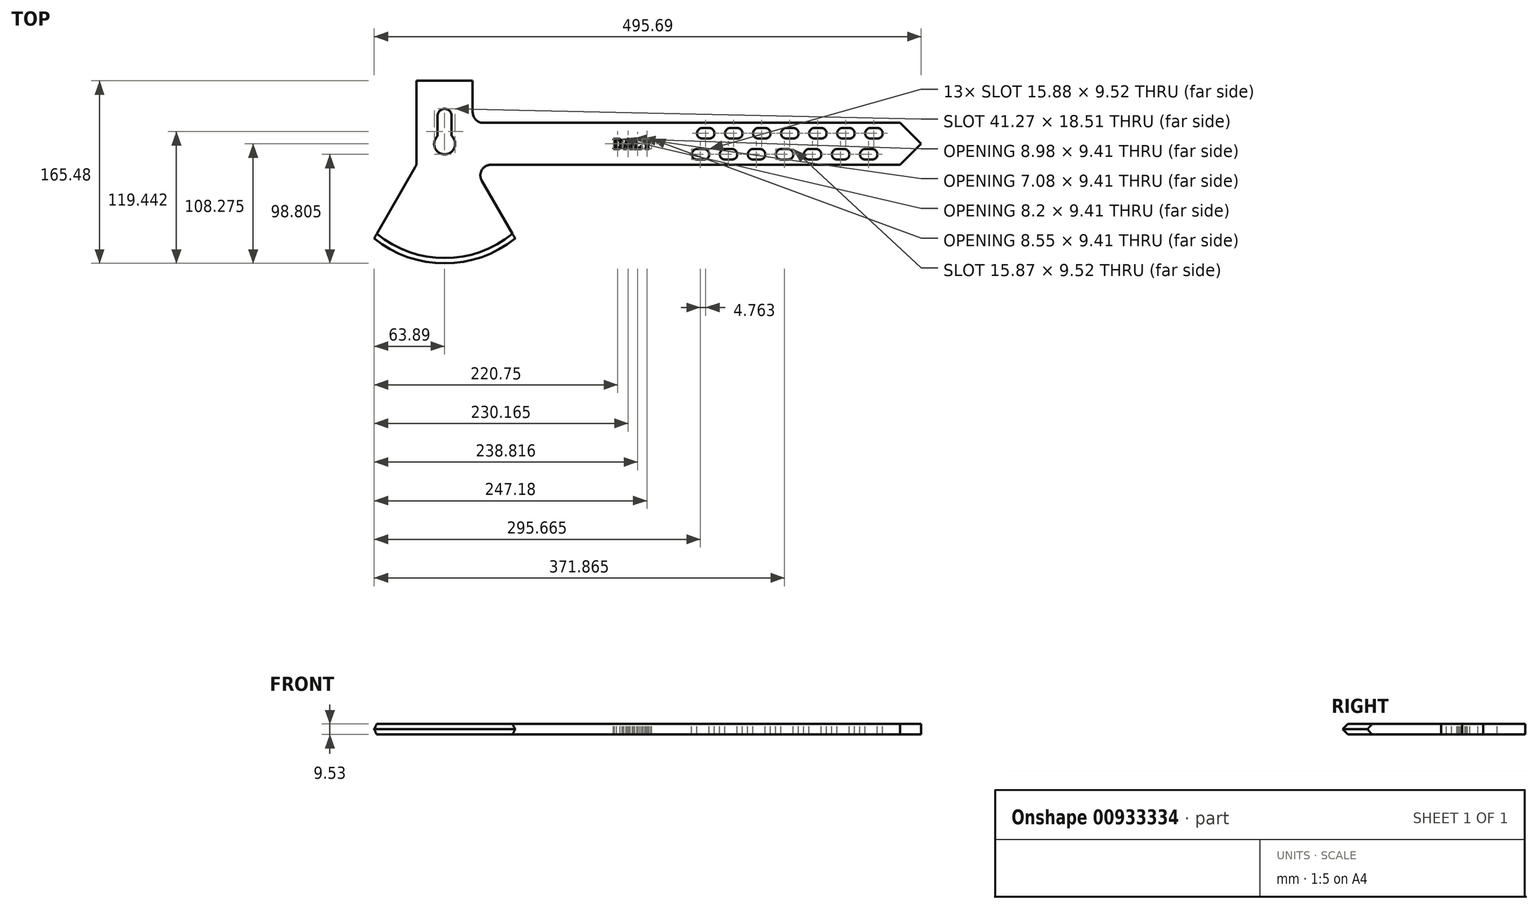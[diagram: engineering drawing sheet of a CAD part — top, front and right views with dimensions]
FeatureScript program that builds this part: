
annotation { "Feature Type Name" : "Feature", "Feature Type Description" : "" }
export const myFeature = defineFeature(function(context is Context, id is Id, definition is map)
    precondition{}
    {
        {
            var Q0;
            Q0=qCreatedBy(makeId("Top.planeOp"),FACE);
            var sketch = newSketch(context, id + "F0", { "sketchPlane" : qUnion([Q0])});
            skLineSegment(sketch, "E0", {"start": v(0, 0) * mm, "end": v(-19.05, 19.05) * mm});
            skLineSegment(sketch, "E1", {"start": v(-19.05, 19.05) * mm, "end": v(-406.4, 19.05) * mm});
            skLineSegment(sketch, "E2", {"start": v(0, 0) * mm, "end": v(-457.2, 0) * mm, "construction": true});
            skLineSegment(sketch, "E3", {"start": v(-457.2, 0) * mm, "end": v(-457.2, 57.15) * mm});
            skLineSegment(sketch, "E4", {"start": v(-457.2, 57.15) * mm, "end": v(-406.4, 57.15) * mm});
            skLineSegment(sketch, "E5", {"start": v(-406.4, 57.15) * mm, "end": v(-406.4, 19.05) * mm});
            skLineSegment(sketch, "E6.MirrorCS", {"start": v(-19.05, -19.05) * mm, "end": v(-406.4, -19.05) * mm});
            skLineSegment(sketch, "E7.MirrorCS", {"start": v(0, 0) * mm, "end": v(-19.05, -19.05) * mm});
            skLineSegment(sketch, "E8", {"start": v(-431.8, 57.15) * mm, "end": v(-431.8, -6.73) * mm, "construction": true});
            skLineSegment(sketch, "E9", {"start": v(-406.4, -19.05) * mm, "end": v(-367.9, -85.73) * mm});
            skLineSegment(sketch, "E10", {"start": v(-457.2, 0) * mm, "end": v(-457.2, -19.05) * mm});
            skLineSegment(sketch, "E11", {"start": v(-457.2, -19.05) * mm, "end": v(-495.7, -85.73) * mm});
            skArc(sketch, "E12", {"start": v(-495.7, -85.73) * mm, "mid": v(-431.8, -108.33) * mm, "end": v(-367.9, -85.73) * mm});
            skSolve(sketch);
        }
        {
            var Q0;
            Q0 = qSketchRegion(id + "F0", true);
            extrude(context, id + "F1", {"entities" : qUnion([Q0]), "depth" : 9.52 * mm, "offsetDistance" : 25.4 * mm});
        }
        {
            var Q0;
            Q0=makeQuery(id+"F1.opExtrude","CAP_FACE",FACE,{"disambiguationData":[OSD([sQuery(id+"F0.wireOp",EDGE,"E0"),sQuery(id+"F0.wireOp",EDGE,"E1"),sQuery(id+"F0.wireOp",EDGE,"E3"),sQuery(id+"F0.wireOp",EDGE,"E4"),sQuery(id+"F0.wireOp",EDGE,"E5"),sQuery(id+"F0.wireOp",EDGE,"E6.MirrorCS"),sQuery(id+"F0.wireOp",EDGE,"E7.MirrorCS"),sQuery(id+"F0.wireOp",EDGE,"E9"),sQuery(id+"F0.wireOp",EDGE,"E10"),sQuery(id+"F0.wireOp",EDGE,"E11"),sQuery(id+"F0.wireOp",EDGE,"E12")])],"isStart":false});
            var sketch = newSketch(context, id + "F2", { "sketchPlane" : qUnion([Q0])});
            skText(sketch, "E13", { "text": "DALY", "fontName": "RobotoSlab-Bold.ttf"});
            skPoint(sketch, "E14", {"position": v(-243.44, 0) * mm});
            skLineSegment(sketch, "E15", {"start": v(-243.44, 0) * mm, "end": v(0, 0) * mm});
            const initialGuessF2  = {"E13": [-0.2794, -0.00476, 1, 0, 0.00953]};
            skSetInitialGuess(sketch, initialGuessF2);
            skSolve(sketch);
        }
        {
            var Q0;
            Q0 = qSketchRegion(id + "F2", true);
            extrude(context, id + "F3", {"entities" : qUnion([Q0]), "operationType" : NewBodyOperationType.REMOVE, "oppositeDirection" : true, "depth" : 25.4 * mm, "offsetDistance" : 25.4 * mm});
        }
        {
            var Q0;
            {var subQ0=sQuery(id+"F0.wireOp",EDGE,"E11");var subQ1=sQuery(id+"F0.wireOp",EDGE,"E9");var subQ2=sQuery(id+"F0.wireOp",EDGE,"E7.MirrorCS");var subQ3=sQuery(id+"F0.wireOp",EDGE,"E6.MirrorCS");var subQ4=sQuery(id+"F0.wireOp",EDGE,"E5");var subQ5=sQuery(id+"F0.wireOp",EDGE,"E12");var subQ6=sQuery(id+"F0.wireOp",EDGE,"E0");var subQ7=sQuery(id+"F0.wireOp",EDGE,"E4");var subQ8=sQuery(id+"F0.wireOp",EDGE,"E1");var subQ9=sQuery(id+"F0.wireOp",EDGE,"E10");var subQ10=sQuery(id+"F0.wireOp",EDGE,"E3");Q0=makeQuery(id+"F3.boolean.opBoolean","SPLIT",FACE,{"disambiguationData":[TD([makeQuery(id+"F1.opExtrude","SWEPT_FACE",FACE,{"disambiguationData":[OSD([subQ6])]})])],"derivedFrom":makeQuery(id+"F1.opExtrude","CAP_FACE",FACE,{"disambiguationData":[OSD([subQ6,subQ8,subQ10,subQ7,subQ4,subQ3,subQ2,subQ1,subQ9,subQ0,subQ5])],"isStart":false})});}
            var sketch = newSketch(context, id + "F4", { "sketchPlane" : qUnion([Q0])});
            skLineSegment(sketch, "E16", {"start": v(0, 0) * mm, "end": v(-203.2, 0) * mm, "construction": true});
            skLineSegment(sketch, "E17", {"start": v(-198.44, 9.52) * mm, "end": v(-192.09, 9.52) * mm});
            skLineSegment(sketch, "E18", {"start": v(-203.2, -9.53) * mm, "end": v(-196.85, -9.53) * mm});
            skArc(sketch, "E19.0.startCap", {"start": v(-198.44, 4.76) * mm, "mid": v(-203.2, 9.52) * mm, "end": v(-198.44, 14.29) * mm});
            skArc(sketch, "E19.0.endCap", {"start": v(-192.09, 14.29) * mm, "mid": v(-187.33, 9.52) * mm, "end": v(-192.09, 4.76) * mm});
            skLineSegment(sketch, "E19.0.left", {"start": v(-198.44, 14.29) * mm, "end": v(-192.09, 14.29) * mm});
            skLineSegment(sketch, "E19.0.right", {"start": v(-198.44, 4.76) * mm, "end": v(-192.09, 4.76) * mm});
            skArc(sketch, "E19.1.startCap", {"start": v(-203.2, -14.29) * mm, "mid": v(-207.96, -9.53) * mm, "end": v(-203.2, -4.76) * mm});
            skArc(sketch, "E19.1.endCap", {"start": v(-196.85, -4.76) * mm, "mid": v(-192.09, -9.53) * mm, "end": v(-196.85, -14.29) * mm});
            skLineSegment(sketch, "E19.1.left", {"start": v(-203.2, -4.76) * mm, "end": v(-196.85, -4.76) * mm});
            skLineSegment(sketch, "E19.1.right", {"start": v(-203.2, -14.29) * mm, "end": v(-196.85, -14.29) * mm});
            skArc(sketch, "E20.1.0.0", {"start": v(-166.69, 14.29) * mm, "mid": v(-161.93, 9.52) * mm, "end": v(-166.69, 4.76) * mm});
            skLineSegment(sketch, "E20.1.0.1", {"start": v(-173.04, 14.29) * mm, "end": v(-166.69, 14.29) * mm});
            skArc(sketch, "E20.1.0.2", {"start": v(-173.04, 4.76) * mm, "mid": v(-177.8, 9.52) * mm, "end": v(-173.04, 14.29) * mm});
            skLineSegment(sketch, "E20.1.0.3", {"start": v(-173.04, 4.76) * mm, "end": v(-166.69, 4.76) * mm});
            skLineSegment(sketch, "E20.1.0.4", {"start": v(-177.8, -4.76) * mm, "end": v(-171.45, -4.76) * mm});
            skArc(sketch, "E20.1.0.5", {"start": v(-171.45, -4.76) * mm, "mid": v(-166.69, -9.53) * mm, "end": v(-171.45, -14.29) * mm});
            skLineSegment(sketch, "E20.1.0.6", {"start": v(-177.8, -14.29) * mm, "end": v(-171.45, -14.29) * mm});
            skArc(sketch, "E20.1.0.7", {"start": v(-177.8, -14.29) * mm, "mid": v(-182.56, -9.53) * mm, "end": v(-177.8, -4.76) * mm});
            skArc(sketch, "E20.2.0.0", {"start": v(-141.29, 14.29) * mm, "mid": v(-136.53, 9.52) * mm, "end": v(-141.29, 4.76) * mm});
            skLineSegment(sketch, "E20.2.0.1", {"start": v(-147.64, 14.29) * mm, "end": v(-141.29, 14.29) * mm});
            skArc(sketch, "E20.2.0.2", {"start": v(-147.64, 4.76) * mm, "mid": v(-152.4, 9.52) * mm, "end": v(-147.64, 14.29) * mm});
            skLineSegment(sketch, "E20.2.0.3", {"start": v(-147.64, 4.76) * mm, "end": v(-141.29, 4.76) * mm});
            skLineSegment(sketch, "E20.2.0.4", {"start": v(-152.4, -4.76) * mm, "end": v(-146.05, -4.76) * mm});
            skArc(sketch, "E20.2.0.5", {"start": v(-146.05, -4.76) * mm, "mid": v(-141.29, -9.53) * mm, "end": v(-146.05, -14.29) * mm});
            skLineSegment(sketch, "E20.2.0.6", {"start": v(-152.4, -14.29) * mm, "end": v(-146.05, -14.29) * mm});
            skArc(sketch, "E20.2.0.7", {"start": v(-152.4, -14.29) * mm, "mid": v(-157.16, -9.53) * mm, "end": v(-152.4, -4.76) * mm});
            skArc(sketch, "E20.3.0.0", {"start": v(-115.89, 14.29) * mm, "mid": v(-111.12, 9.52) * mm, "end": v(-115.89, 4.76) * mm});
            skLineSegment(sketch, "E20.3.0.1", {"start": v(-122.24, 14.29) * mm, "end": v(-115.89, 14.29) * mm});
            skArc(sketch, "E20.3.0.2", {"start": v(-122.24, 4.76) * mm, "mid": v(-127, 9.52) * mm, "end": v(-122.24, 14.29) * mm});
            skLineSegment(sketch, "E20.3.0.3", {"start": v(-122.24, 4.76) * mm, "end": v(-115.89, 4.76) * mm});
            skLineSegment(sketch, "E20.3.0.4", {"start": v(-127, -4.76) * mm, "end": v(-120.65, -4.76) * mm});
            skArc(sketch, "E20.3.0.5", {"start": v(-120.65, -4.76) * mm, "mid": v(-115.89, -9.53) * mm, "end": v(-120.65, -14.29) * mm});
            skLineSegment(sketch, "E20.3.0.6", {"start": v(-127, -14.29) * mm, "end": v(-120.65, -14.29) * mm});
            skArc(sketch, "E20.3.0.7", {"start": v(-127, -14.29) * mm, "mid": v(-131.76, -9.53) * mm, "end": v(-127, -4.76) * mm});
            skArc(sketch, "E20.4.0.0", {"start": v(-90.49, 14.29) * mm, "mid": v(-85.72, 9.52) * mm, "end": v(-90.49, 4.76) * mm});
            skLineSegment(sketch, "E20.4.0.1", {"start": v(-96.84, 14.29) * mm, "end": v(-90.49, 14.29) * mm});
            skArc(sketch, "E20.4.0.2", {"start": v(-96.84, 4.76) * mm, "mid": v(-101.6, 9.52) * mm, "end": v(-96.84, 14.29) * mm});
            skLineSegment(sketch, "E20.4.0.3", {"start": v(-96.84, 4.76) * mm, "end": v(-90.49, 4.76) * mm});
            skLineSegment(sketch, "E20.4.0.4", {"start": v(-101.6, -4.76) * mm, "end": v(-95.25, -4.76) * mm});
            skArc(sketch, "E20.4.0.5", {"start": v(-95.25, -4.76) * mm, "mid": v(-90.49, -9.53) * mm, "end": v(-95.25, -14.29) * mm});
            skLineSegment(sketch, "E20.4.0.6", {"start": v(-101.6, -14.29) * mm, "end": v(-95.25, -14.29) * mm});
            skArc(sketch, "E20.4.0.7", {"start": v(-101.6, -14.29) * mm, "mid": v(-106.36, -9.53) * mm, "end": v(-101.6, -4.76) * mm});
            skArc(sketch, "E20.5.0.0", {"start": v(-65.09, 14.29) * mm, "mid": v(-60.32, 9.52) * mm, "end": v(-65.09, 4.76) * mm});
            skLineSegment(sketch, "E20.5.0.1", {"start": v(-71.44, 14.29) * mm, "end": v(-65.09, 14.29) * mm});
            skArc(sketch, "E20.5.0.2", {"start": v(-71.44, 4.76) * mm, "mid": v(-76.2, 9.52) * mm, "end": v(-71.44, 14.29) * mm});
            skLineSegment(sketch, "E20.5.0.3", {"start": v(-71.44, 4.76) * mm, "end": v(-65.09, 4.76) * mm});
            skLineSegment(sketch, "E20.5.0.4", {"start": v(-76.2, -4.76) * mm, "end": v(-69.85, -4.76) * mm});
            skArc(sketch, "E20.5.0.5", {"start": v(-69.85, -4.76) * mm, "mid": v(-65.09, -9.53) * mm, "end": v(-69.85, -14.29) * mm});
            skLineSegment(sketch, "E20.5.0.6", {"start": v(-76.2, -14.29) * mm, "end": v(-69.85, -14.29) * mm});
            skArc(sketch, "E20.5.0.7", {"start": v(-76.2, -14.29) * mm, "mid": v(-80.96, -9.53) * mm, "end": v(-76.2, -4.76) * mm});
            skArc(sketch, "E20.6.0.0", {"start": v(-39.69, 14.29) * mm, "mid": v(-34.92, 9.52) * mm, "end": v(-39.69, 4.76) * mm});
            skLineSegment(sketch, "E20.6.0.1", {"start": v(-46.04, 14.29) * mm, "end": v(-39.69, 14.29) * mm});
            skArc(sketch, "E20.6.0.2", {"start": v(-46.04, 4.76) * mm, "mid": v(-50.8, 9.52) * mm, "end": v(-46.04, 14.29) * mm});
            skLineSegment(sketch, "E20.6.0.3", {"start": v(-46.04, 4.76) * mm, "end": v(-39.69, 4.76) * mm});
            skLineSegment(sketch, "E20.6.0.4", {"start": v(-50.8, -4.76) * mm, "end": v(-44.45, -4.76) * mm});
            skArc(sketch, "E20.6.0.5", {"start": v(-44.45, -4.76) * mm, "mid": v(-39.69, -9.53) * mm, "end": v(-44.45, -14.29) * mm});
            skLineSegment(sketch, "E20.6.0.6", {"start": v(-50.8, -14.29) * mm, "end": v(-44.45, -14.29) * mm});
            skArc(sketch, "E20.6.0.7", {"start": v(-50.8, -14.29) * mm, "mid": v(-55.56, -9.53) * mm, "end": v(-50.8, -4.76) * mm});
            skLineSegment(sketch, "E20.direction1", {"start": v(-192.09, 4.76) * mm, "end": v(-166.69, 4.76) * mm, "construction": true});
            skSolve(sketch);
        }
        {
            var Q0;
            Q0 = qSketchRegion(id + "F4", true);
            extrude(context, id + "F5", {"entities" : qUnion([Q0]), "operationType" : NewBodyOperationType.REMOVE, "oppositeDirection" : true, "depth" : 25.4 * mm, "offsetDistance" : 25.4 * mm});
        }
        {
            var Q0;
            Q0=makeQuery(id+"F1.opExtrude","SWEPT_EDGE",EDGE,{"disambiguationData":[OSD([sQuery(id+"F0.wireOp",EDGE,"E1"),sQuery(id+"F0.wireOp",EDGE,"E5")])]});
            var Q1;
            Q1=makeQuery(id+"F1.opExtrude","SWEPT_EDGE",EDGE,{"disambiguationData":[OSD([sQuery(id+"F0.wireOp",EDGE,"E6.MirrorCS"),sQuery(id+"F0.wireOp",EDGE,"E9")])]});
            var Q2;
            Q2=makeQuery(id+"F1.opExtrude","SWEPT_EDGE",EDGE,{"disambiguationData":[OSD([sQuery(id+"F0.wireOp",EDGE,"E10"),sQuery(id+"F0.wireOp",EDGE,"E11")])]});
            fillet(context, id + "F6", {"entities" : qUnion([Q0, Q1, Q2]), "radius" : 9.52 * mm, "tangentPropagation" : true, "allowEdgeOverflow" : false});
        }
        {
            var Q0;
            {var subQ0=sQuery(id+"F0.wireOp",EDGE,"E11");var subQ1=sQuery(id+"F0.wireOp",EDGE,"E9");var subQ2=sQuery(id+"F0.wireOp",EDGE,"E7.MirrorCS");var subQ3=sQuery(id+"F0.wireOp",EDGE,"E6.MirrorCS");var subQ4=sQuery(id+"F0.wireOp",EDGE,"E5");var subQ5=sQuery(id+"F0.wireOp",EDGE,"E12");var subQ6=sQuery(id+"F0.wireOp",EDGE,"E0");var subQ7=sQuery(id+"F0.wireOp",EDGE,"E4");var subQ8=sQuery(id+"F0.wireOp",EDGE,"E1");var subQ9=sQuery(id+"F0.wireOp",EDGE,"E10");var subQ10=sQuery(id+"F0.wireOp",EDGE,"E3");Q0=makeQuery(id+"F3.boolean.opBoolean","SPLIT",FACE,{"disambiguationData":[TD([makeQuery(id+"F1.opExtrude","SWEPT_FACE",FACE,{"disambiguationData":[OSD([subQ6])]})])],"derivedFrom":makeQuery(id+"F1.opExtrude","CAP_FACE",FACE,{"disambiguationData":[OSD([subQ6,subQ8,subQ10,subQ7,subQ4,subQ3,subQ2,subQ1,subQ9,subQ0,subQ5])],"isStart":false})});}
            var sketch = newSketch(context, id + "F7", { "sketchPlane" : qUnion([Q0])});
            skLineSegment(sketch, "E21", {"start": v(-431.8, 57.15) * mm, "end": v(-431.8, 25.4) * mm, "construction": true});
            skLineSegment(sketch, "E22", {"start": v(-431.8, 25.4) * mm, "end": v(-431.8, 0) * mm, "construction": true});
            skArc(sketch, "E23.0.startCap", {"start": v(-438.15, 25.4) * mm, "mid": v(-431.8, 31.75) * mm, "end": v(-425.45, 25.4) * mm});
            skArc(sketch, "E24", {"start": v(-441.33, 0) * mm, "mid": v(-431.8, -9.53) * mm, "end": v(-422.28, 0) * mm});
            skLineSegment(sketch, "E25", {"start": v(-438.15, 25.4) * mm, "end": v(-438.15, 7.1) * mm});
            skArc(sketch, "E26", {"start": v(-441.33, 0) * mm, "mid": v(-440.5, 3.89) * mm, "end": v(-438.15, 7.1) * mm});
            skLineSegment(sketch, "E27.MirrorCS", {"start": v(-425.45, 25.4) * mm, "end": v(-425.45, 7.1) * mm});
            skArc(sketch, "E28.MirrorCS", {"start": v(-422.28, 0) * mm, "mid": v(-423.1, 3.89) * mm, "end": v(-425.45, 7.1) * mm});
            skSolve(sketch);
        }
        {
            var Q0;
            Q0 = qSketchRegion(id + "F7", true);
            extrude(context, id + "F8", {"entities" : qUnion([Q0]), "operationType" : NewBodyOperationType.REMOVE, "oppositeDirection" : true, "depth" : 25.4 * mm, "offsetDistance" : 25.4 * mm});
        }
        {
            var Q0;
            Q0=makeQuery(id+"F1.opExtrude","CAP_EDGE",EDGE,{"disambiguationData":[OSD([sQuery(id+"F0.wireOp",EDGE,"E12")])],"isStart":false});
            var Q1;
            Q1=makeQuery(id+"F1.opExtrude","CAP_EDGE",EDGE,{"disambiguationData":[OSD([sQuery(id+"F0.wireOp",EDGE,"E12")])],"isStart":true});
            chamfer(context, id + "F9", {"entities" : qUnion([Q0, Q1]), "chamferType" : ChamferType.OFFSET_ANGLE, "width" : 4.76 * mm, "oppositeDirection" : false, "angle" : 45 * degree, "tangentPropagation" : true});
        }
    });
